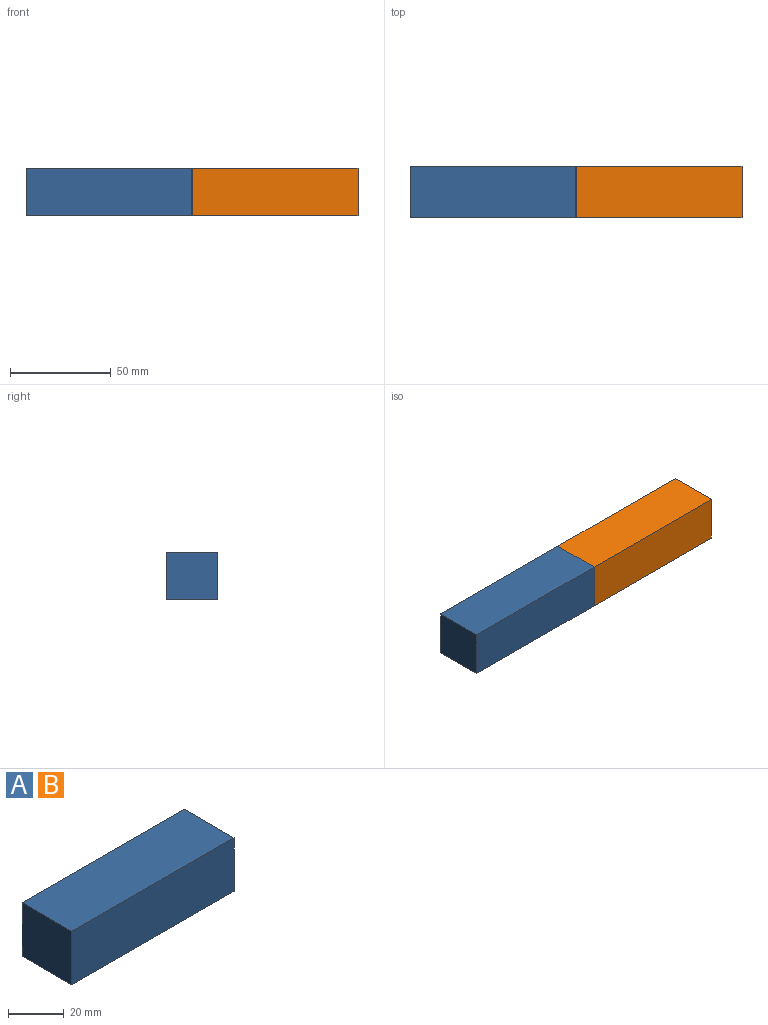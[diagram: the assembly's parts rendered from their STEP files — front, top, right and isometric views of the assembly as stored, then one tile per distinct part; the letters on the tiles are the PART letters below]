
ASSEMBLY  parts=2 mates=1
PART A: 6 faces, bbox 82.4x25.4x23.5 mm
  f0: plane 25.4x23.54mm, normal (-1,0,0), area 598mm2, adj f1,f3,f4,f5
  f1: plane 82.42x25.4mm, normal (0,0,-1), area 2093.6mm2, adj f0,f2,f3,f4
  f2: plane 25.4x23.54mm, normal (1,0,0), area 598mm2, adj f1,f3,f4,f5
  f3: plane 82.42x23.54mm, normal (0,-1,0), area 1940.6mm2, adj f0,f1,f2,f5
  f4: plane 82.42x23.54mm, normal (0,1,0), area 1940.6mm2, adj f0,f1,f2,f5
  f5: plane 82.42x25.4mm, normal (0,0,1), area 2093.6mm2, adj f0,f2,f3,f4
PART B: same geometry as A
PLACE A t=(-129.75,19.61,224.16)mm
PLACE B t=(-47.33,19.61,224.16)mm
MATE fastened A.f2 <-> B.f0  axis (1,0,0) through (-86.83,6.91,235.93)mm
